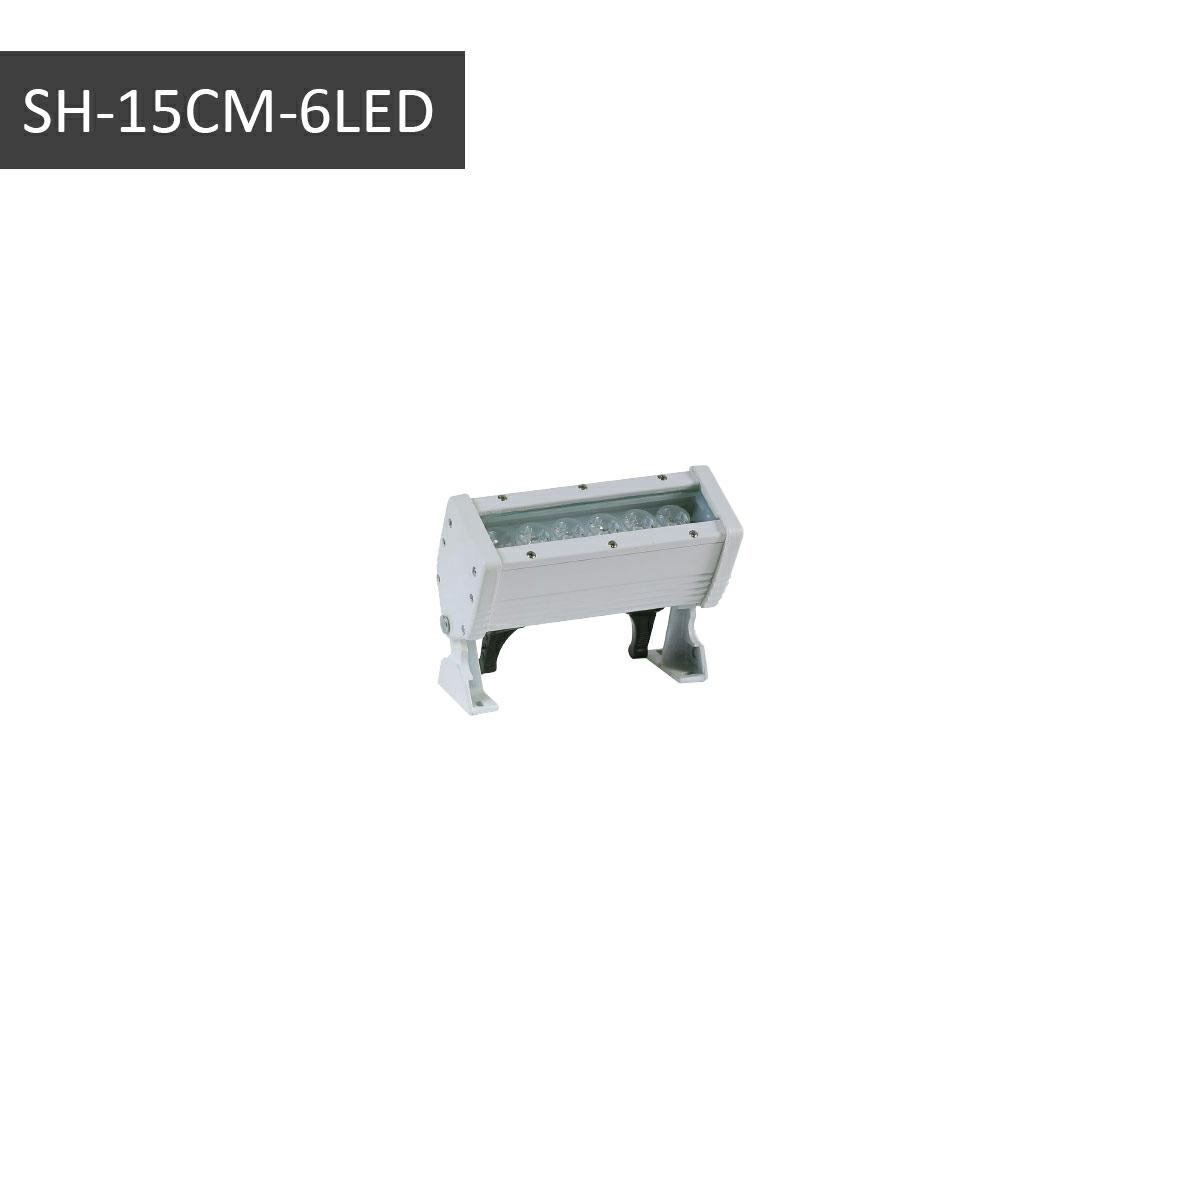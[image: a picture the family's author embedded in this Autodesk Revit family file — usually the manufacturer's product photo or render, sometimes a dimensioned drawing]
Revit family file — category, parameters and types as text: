
# Revit family: Sh-6418
name_source: partatom
category: Lighting Fixtures
revit_build: Autodesk Revit 2017 (Build: 20160225_1515(x64)
units: mm (PartAtom-declared; Revit-internal decimal feet)

## family parameters
Always vertical = Yes
Cut with Voids When Loaded = No
Light Source = No
OmniClass Number = 23.80.70.00
OmniClass Title = Lighting
Part Type = Normal
Room Calculation Point = No
Round Connector Dimension = Use Diameter
Shared = No
Work Plane-Based = No

## types (4) — shared parameters
Beam Angle = 30.00°
Body Material = Aluminium
Body color = aluminium
Flicker = FREE Flicker
IP = IP65
Lamp = LED
Length = 29.50 cm
Manufacturer = SHOA
Model = Sh-6418
Protection Class = Class I
Type medule = Power led
URL = https://www.shoaco.com
Voltage/Frequency = 230V-50HZ
Width = 17.50 cm
color rendering index(CRI) = 80
consumption current = 0 A
instalation = inground
wattage. = 18 W
website = www.shoaco.com

## per-type parameters (varying)
| type | color temperature |
| Sh-6418(Aluminium Body-2000K-LED) | 2000K |
| Sh-6418(Aluminium Body-3000K-LED) | 3000K |
| Sh-6418(Aluminium Body-6500K-LED) | 6500K |
| Sh-6418(Aluminium Body-RGB-LED) | RGB |

## geometry (parser evidence)
native form markers: Sweep x3
no freeform markers — native parametric forms only
